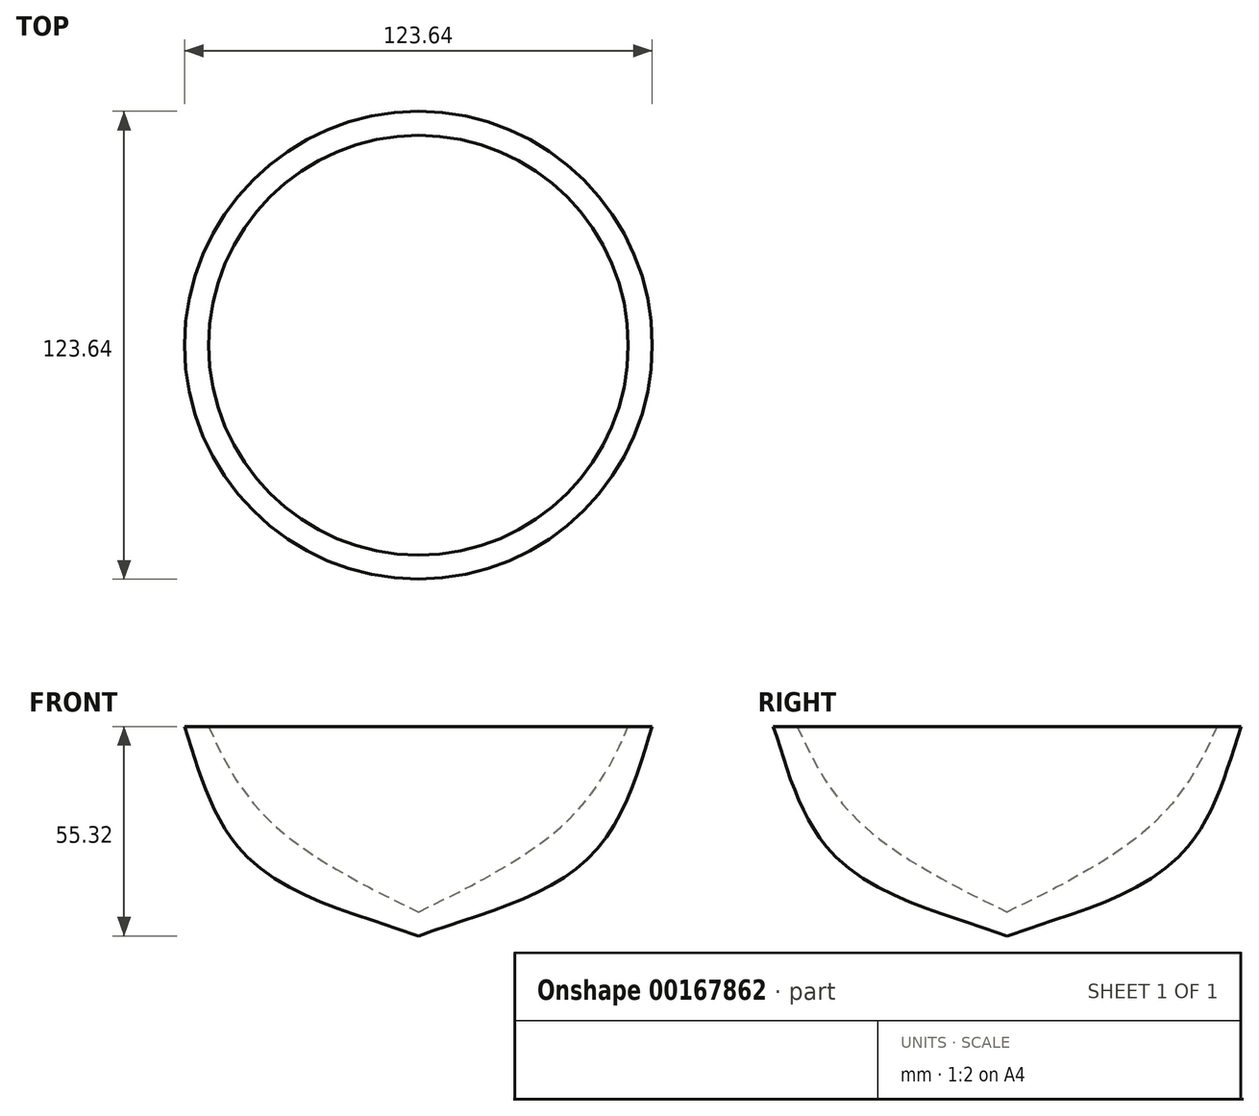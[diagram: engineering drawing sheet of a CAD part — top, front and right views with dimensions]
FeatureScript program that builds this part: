
annotation { "Feature Type Name" : "Feature", "Feature Type Description" : "" }
export const myFeature = defineFeature(function(context is Context, id is Id, definition is map)
    precondition{}
    {
        {
            var Q0;
            Q0=qCreatedBy(makeId("Front.planeOp"),FACE);
            var sketch = newSketch(context, id + "F0", { "sketchPlane" : qUnion([Q0])});
            skLineSegment(sketch, "E0", {"start": v(0, 0) * mm, "end": v(0, 6.35) * mm});
            skFitSpline(sketch, "E1", {"points": [v(0, 6.35) * mm, v(39.4, 30.44) * mm, v(55.47, 55.32) * mm], "startDerivative": vector(81.97, 39.54) * mm, "endDerivative": vector(25.56, 59.8) * mm});
            skLineSegment(sketch, "E2", {"start": v(55.47, 55.32) * mm, "end": v(61.82, 55.32) * mm});
            skFitSpline(sketch, "E3", {"points": [v(0, 0) * mm, v(45.48, 21.07) * mm, v(61.82, 55.32) * mm], "startDerivative": vector(85.47, 31.25) * mm, "endDerivative": vector(20.9, 61.57) * mm});
            skSolve(sketch);
        }
        {
            var Q0;
            Q0 = qSketchRegion(id + "F0", true);
            var Q1;
            Q1=sQuery(id+"F0.wireOp",EDGE,"E0");
            revolve(context, id + "F1", {"entities" : qUnion([Q0]), "axis" : qUnion([Q1]), "revolveType" : RevolveType.FULL});
        }
    });
